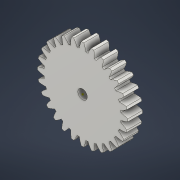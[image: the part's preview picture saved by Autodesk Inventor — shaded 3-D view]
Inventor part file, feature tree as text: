
AUTODESK INVENTOR PART (.ipt)
format: ipt  version: 2022.2 (Build 262287030, 287C)  size: 279,552 bytes
history: native  units: mm (DEFAULTED — no unit token found)
features: sketch x4, plane x3, other x3, extrude x2
ambient origin geometry x8: Origin, YZ Plane, XZ Plane, XY Plane, X Axis, Y Axis, Z Axis, Center Point
bodies: Solid1 (feature_tree)
feature tree (12):
  extrude  "Extrusion1"  Depth=10.0mm TaperAngle=0.0deg
  plane  "Work Plane2"
  plane  "Work Plane8"
  plane  "Work Plane9"
  other  "Spur Gear"
  sketch  "Sketch3"  dims[d16=40.43451mm]
  extrude  "Extrusion2"  Depth=10.0mm TaperAngle=0.0deg
  sketch  "Sketch1"  dims[d0=60.86902mm d1=10.0mm d2=0.0mm]
  sketch  "Sketch2"  dims[d3=56.0mm d4=10.0mm d5=0.0mm]
  other  "Srf1"
  sketch  "Sketch4"  dims[d17=0.0mm d34=1.121997mm d39=0.0mm d41=0.0mm d43=40.43451mm d46=40.43451mm d47=0.0mm d48=0.0mm d49=6.35mm d50=0.0mm d51=0.0mm]
  other  "Pitch Diameter"
